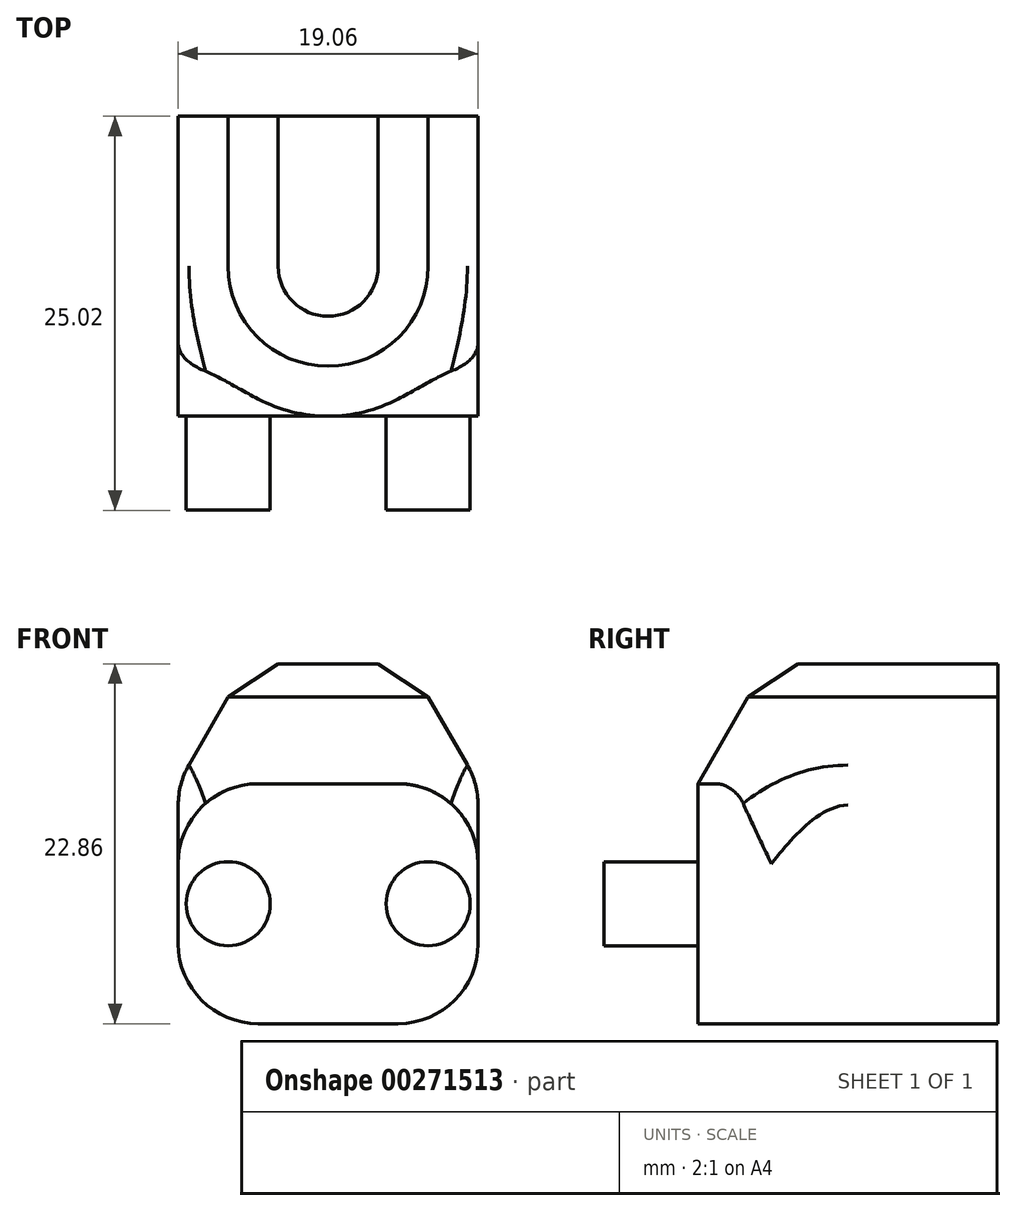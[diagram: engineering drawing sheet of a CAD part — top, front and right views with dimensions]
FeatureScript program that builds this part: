
annotation { "Feature Type Name" : "Feature", "Feature Type Description" : "" }
export const myFeature = defineFeature(function(context is Context, id is Id, definition is map)
    precondition{}
    {
        {
            var Q0;
            Q0=qCreatedBy(makeId("Right.planeOp"),FACE);
            var sketch = newSketch(context, id + "F0", { "sketchPlane" : qUnion([Q0])});
            skLineSegment(sketch, "E0", {"start": v(-19.05, 0) * mm, "end": v(-19.05, 15.24) * mm});
            skLineSegment(sketch, "E1", {"start": v(0, 15.24) * mm, "end": v(0, 0) * mm});
            skLineSegment(sketch, "E2", {"start": v(0, 0) * mm, "end": v(-19.05, 0) * mm});
            skLineSegment(sketch, "E3", {"start": v(-19.05, 15.24) * mm, "end": v(0, 15.24) * mm});
            skSolve(sketch);
        }
        {
            var Q0;
            Q0=qSketchRegion(id+"F0",true);
            extrude(context, id + "F1", {"entities" : qUnion([Q0]), "endBound" : BoundingType.SYMMETRIC, "depth" : 19.05 * mm});
        }
        {
            var Q0;
            Q0=makeQuery(id+"F1.opExtrude","SWEPT_FACE",FACE,{"disambiguationData":[OSD([sQuery(id+"F0.wireOp",EDGE,"E0")])]});
            var sketch = newSketch(context, id + "F2", { "sketchPlane" : qUnion([Q0])});
            skCircle(sketch, "E4", {"center": v(6.35, 7.62) * mm, "radius": 2.67 * mm});
            skPoint(sketch, "E4.centerSnap0", {"position": v(10.15, 7.62) * mm});
            skCircle(sketch, "E5", {"center": v(-6.35, 7.62) * mm, "radius": 2.67 * mm});
            skSolve(sketch);
        }
        {
            var Q0;
            Q0=qSketchRegion(id+"F2",true);
            extrude(context, id + "F3", {"entities" : qUnion([Q0]), "operationType" : NewBodyOperationType.ADD, "depth" : 5.97 * mm});
        }
        {
            var Q0;
            Q0=qCreatedBy(makeId("Right.planeOp"),FACE);
            var sketch = newSketch(context, id + "F4", { "sketchPlane" : qUnion([Q0])});
            skLineSegment(sketch, "E6", {"start": v(-9.53, 15.24) * mm, "end": v(-9.53, 22.86) * mm});
            skLineSegment(sketch, "E7", {"start": v(-9.53, 22.86) * mm, "end": v(-12.7, 22.86) * mm});
            skLineSegment(sketch, "E8", {"start": v(-12.7, 22.86) * mm, "end": v(-15.88, 20.74) * mm});
            skLineSegment(sketch, "E9", {"start": v(-15.88, 20.74) * mm, "end": v(-19.05, 15.24) * mm});
            skLineSegment(sketch, "E10", {"start": v(-9.53, 15.24) * mm, "end": v(-19.05, 15.24) * mm});
            skSolve(sketch);
        }
        {
            var Q0;
            Q0=makeQuery(id+"F4.imprint","IMPRINT",FACE,{"disambiguationData":[TD([[makeQuery(id+"F4.imprint","IMPRINT",EDGE,{"derivedFrom":sQuery(id+"F4.wireOp",EDGE,"E6")}),1.0]])]});
            var Q1;
            Q1=sQuery(id+"F4.wireOp",EDGE,"E6");
            revolve(context, id + "F5", {"operationType" : NewBodyOperationType.ADD, "entities" : qUnion([Q0]), "axis" : qUnion([Q1]), "revolveType" : RevolveType.FULL});
        }
        {
            var Q0;
            Q0=makeQuery(id+"F1.opExtrude","SWEPT_FACE",FACE,{"disambiguationData":[OSD([sQuery(id+"F0.wireOp",EDGE,"E1")])]});
            var sketch = newSketch(context, id + "F6", { "sketchPlane" : qUnion([Q0])});
            skLineSegment(sketch, "E11", {"start": v(-9.53, 0) * mm, "end": v(9.53, 0) * mm});
            skLineSegment(sketch, "E12", {"start": v(9.53, 0) * mm, "end": v(9.53, 15.24) * mm});
            skLineSegment(sketch, "E13", {"start": v(9.53, 15.24) * mm, "end": v(6.35, 20.74) * mm});
            skLineSegment(sketch, "E14", {"start": v(6.35, 20.74) * mm, "end": v(3.18, 22.86) * mm});
            skLineSegment(sketch, "E15", {"start": v(3.18, 22.86) * mm, "end": v(-3.18, 22.86) * mm});
            skLineSegment(sketch, "E16", {"start": v(-3.18, 22.86) * mm, "end": v(-6.35, 20.74) * mm});
            skLineSegment(sketch, "E17", {"start": v(-6.35, 20.74) * mm, "end": v(-9.53, 15.24) * mm});
            skLineSegment(sketch, "E18", {"start": v(-9.53, 15.24) * mm, "end": v(-9.53, 0) * mm});
            skSolve(sketch);
        }
        {
            var Q0;
            Q0=makeQuery(id+"F6.imprint","IMPRINT",FACE,{"disambiguationData":[TD([[makeQuery(id+"F6.imprint","IMPRINT",EDGE,{"derivedFrom":sQuery(id+"F6.wireOp",EDGE,"E13")}),1.0]])]});
            var Q1;
            Q1=makeQuery(id+"F1.opExtrude","SWEPT_BODY",BODY,{"disambiguationData":[OSD([sQuery(id+"F0.wireOp",EDGE,"E0"),sQuery(id+"F0.wireOp",EDGE,"E1"),sQuery(id+"F0.wireOp",EDGE,"E2"),sQuery(id+"F0.wireOp",EDGE,"E3")])]});
            extrude(context, id + "F7", {"entities" : qUnion([Q0]), "operationType" : NewBodyOperationType.ADD, "endBound" : BoundingType.UP_TO_BODY, "oppositeDirection" : true, "endBoundEntityBody" : qUnion([Q1]), "depth" : 25.4 * mm});
        }
        {
            var Q0;
            {var subQ0=sQuery(id+"F0.wireOp",EDGE,"E0");var subQ1=sQuery(id+"F0.wireOp",EDGE,"E3");Q0=makeQuery(id+"F5.boolean.opBoolean","SPLIT",EDGE,{"disambiguationData":[TD([makeQuery(id+"F1.opExtrude","SWEPT_FACE",FACE,{"disambiguationData":[OSD([subQ0])]})])],"derivedFrom":makeQuery(id+"F1.opExtrude","CAP_EDGE",EDGE,{"disambiguationData":[OSD([subQ1])],"isStart":false})});}
            var Q1;
            {var subQ0=sQuery(id+"F0.wireOp",EDGE,"E0");var subQ1=sQuery(id+"F0.wireOp",EDGE,"E3");Q1=makeQuery(id+"F5.boolean.opBoolean","SPLIT",EDGE,{"disambiguationData":[TD([makeQuery(id+"F1.opExtrude","SWEPT_FACE",FACE,{"disambiguationData":[OSD([subQ0])]})])],"derivedFrom":makeQuery(id+"F1.opExtrude","CAP_EDGE",EDGE,{"disambiguationData":[OSD([subQ1])],"isStart":true})});}
            var Q2;
            Q2=makeQuery(id+"F1.opExtrude","CAP_EDGE",EDGE,{"disambiguationData":[OSD([sQuery(id+"F0.wireOp",EDGE,"E2")])],"isStart":true});
            var Q3;
            Q3=makeQuery(id+"F1.opExtrude","CAP_EDGE",EDGE,{"disambiguationData":[OSD([sQuery(id+"F0.wireOp",EDGE,"E2")])],"isStart":false});
            fillet(context, id + "F8", {"entities" : qUnion([Q0, Q1, Q2, Q3]), "radius" : 5.08 * mm, "tangentPropagation" : true, "allowEdgeOverflow" : false});
        }
    });
